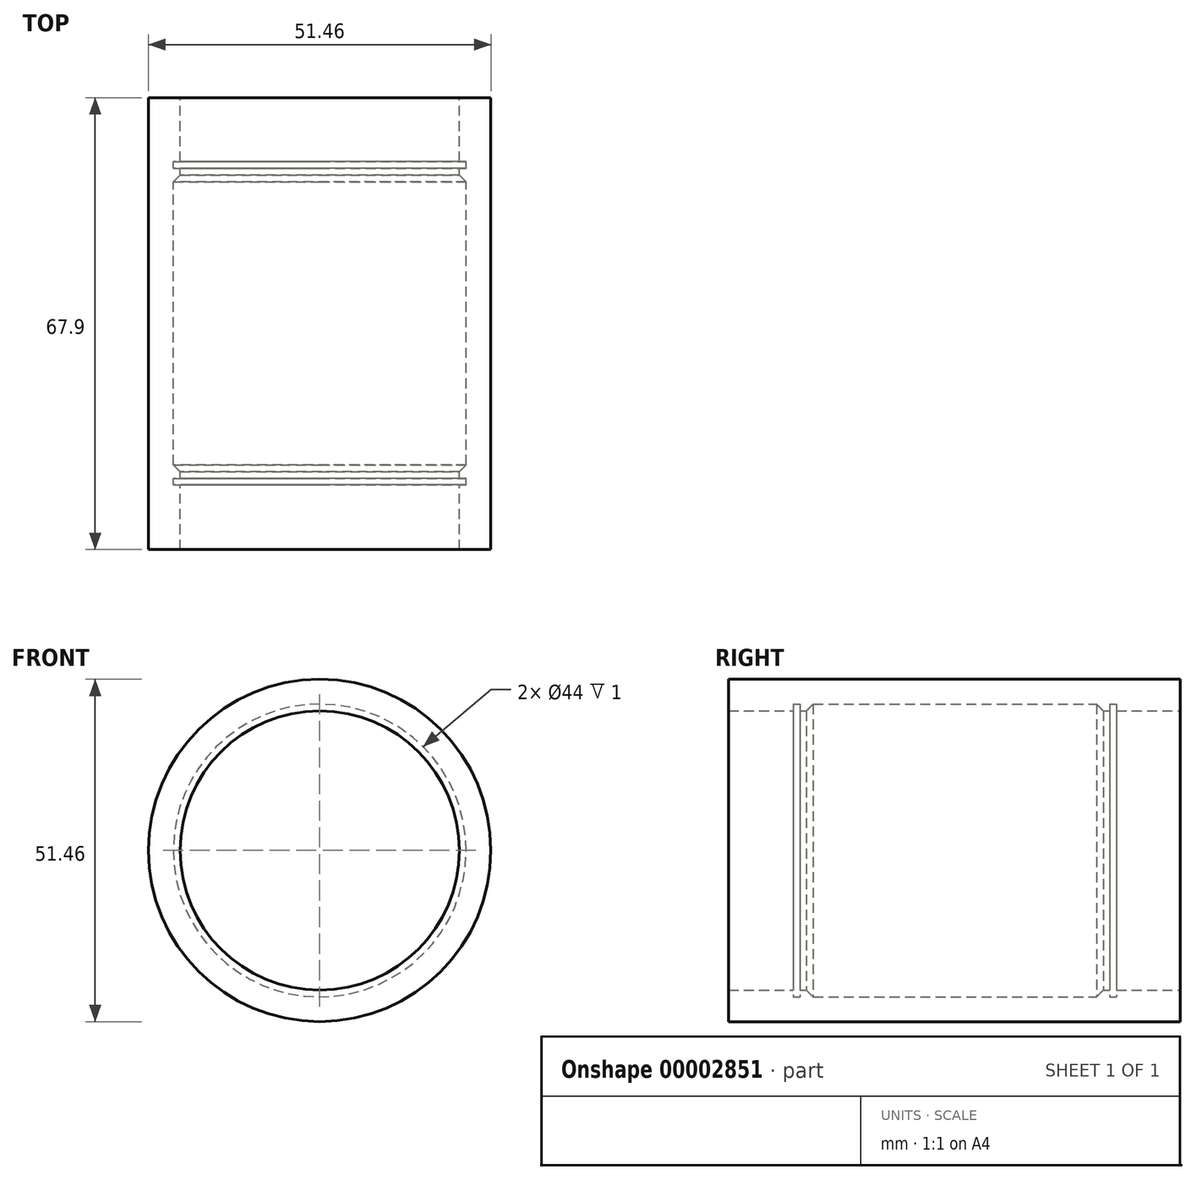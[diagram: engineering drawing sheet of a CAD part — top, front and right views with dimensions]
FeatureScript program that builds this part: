
annotation { "Feature Type Name" : "Feature", "Feature Type Description" : "" }
export const myFeature = defineFeature(function(context is Context, id is Id, definition is map)
    precondition{}
    {
        {
            var Q0;
            Q0=qCreatedBy(makeId("Right.planeOp"),FACE);
            var sketch = newSketch(context, id + "F0", { "sketchPlane" : qUnion([Q0])});
            skLineSegment(sketch, "E0.top", {"start": v(-21.28, 22) * mm, "end": v(0, 22) * mm});
            skLineSegment(sketch, "E1", {"start": v(0, 0) * mm, "end": v(-79.11, 0) * mm, "construction": true});
            skLineSegment(sketch, "E2", {"start": v(-21.28, 22) * mm, "end": v(-22.3, 20.98) * mm});
            skLineSegment(sketch, "E3", {"start": v(-22.3, 20.98) * mm, "end": v(-23.3, 20.98) * mm});
            skLineSegment(sketch, "E4", {"start": v(-23.3, 20.98) * mm, "end": v(-23.3, 22) * mm});
            skLineSegment(sketch, "E5", {"start": v(-23.3, 22) * mm, "end": v(-24.3, 22) * mm});
            skLineSegment(sketch, "E6", {"start": v(-24.3, 22) * mm, "end": v(-24.3, 20.98) * mm});
            skLineSegment(sketch, "E7", {"start": v(-24.3, 20.98) * mm, "end": v(-34, 20.98) * mm});
            skLineSegment(sketch, "E8", {"start": v(-34, 20.98) * mm, "end": v(-34, 25.73) * mm});
            skLineSegment(sketch, "E9", {"start": v(-34, 25.73) * mm, "end": v(0, 25.73) * mm});
            skLineSegment(sketch, "E10", {"start": v(0, 25.73) * mm, "end": v(0, 0) * mm, "construction": true});
            skLineSegment(sketch, "E11", {"start": v(-24.3, 20.98) * mm, "end": v(-23.3, 20.98) * mm, "construction": true});
            skLineSegment(sketch, "E12.0.MirrorCS", {"start": v(24.3, 20.98) * mm, "end": v(23.3, 20.98) * mm, "construction": true});
            skLineSegment(sketch, "E12.1.MirrorCS", {"start": v(23.3, 20.98) * mm, "end": v(23.3, 22) * mm});
            skLineSegment(sketch, "E12.2.MirrorCS", {"start": v(24.3, 22) * mm, "end": v(24.3, 20.98) * mm});
            skLineSegment(sketch, "E12.3.MirrorCS", {"start": v(22.3, 20.98) * mm, "end": v(23.3, 20.98) * mm});
            skLineSegment(sketch, "E12.4.MirrorCS", {"start": v(21.28, 22) * mm, "end": v(22.3, 20.98) * mm});
            skLineSegment(sketch, "E12.5.MirrorCS", {"start": v(23.3, 22) * mm, "end": v(24.3, 22) * mm});
            skLineSegment(sketch, "E12.6.MirrorCS", {"start": v(34, 25.73) * mm, "end": v(0, 25.73) * mm});
            skLineSegment(sketch, "E12.7.MirrorCS", {"start": v(21.28, 22) * mm, "end": v(0, 22) * mm});
            skLineSegment(sketch, "E12.8.MirrorCS", {"start": v(24.3, 20.98) * mm, "end": v(34, 20.98) * mm});
            skLineSegment(sketch, "E12.9.MirrorCS", {"start": v(34, 20.98) * mm, "end": v(34, 25.73) * mm});
            skSolve(sketch);
        }
        {
            var Q0;
            Q0 = qSketchRegion(id + "F0", true);
            var Q1;
            Q1=sQuery(id+"F0.wireOp",EDGE,"E1");
            revolve(context, id + "F1", {"entities" : qUnion([Q0]), "axis" : qUnion([Q1]), "revolveType" : RevolveType.FULL});
        }
        {
            var Q0;
            Q0=makeQuery(id+"F1.opRevolve","SWEPT_FACE",FACE,{"disambiguationData":[OSD([sQuery(id+"F0.wireOp",EDGE,"E12.9.MirrorCS")])]});
            extrude(context, id + "F2", {"entities" : qUnion([Q0]), "operationType" : NewBodyOperationType.REMOVE, "oppositeDirection" : true, "depth" : .1 * mm});
        }
    });
